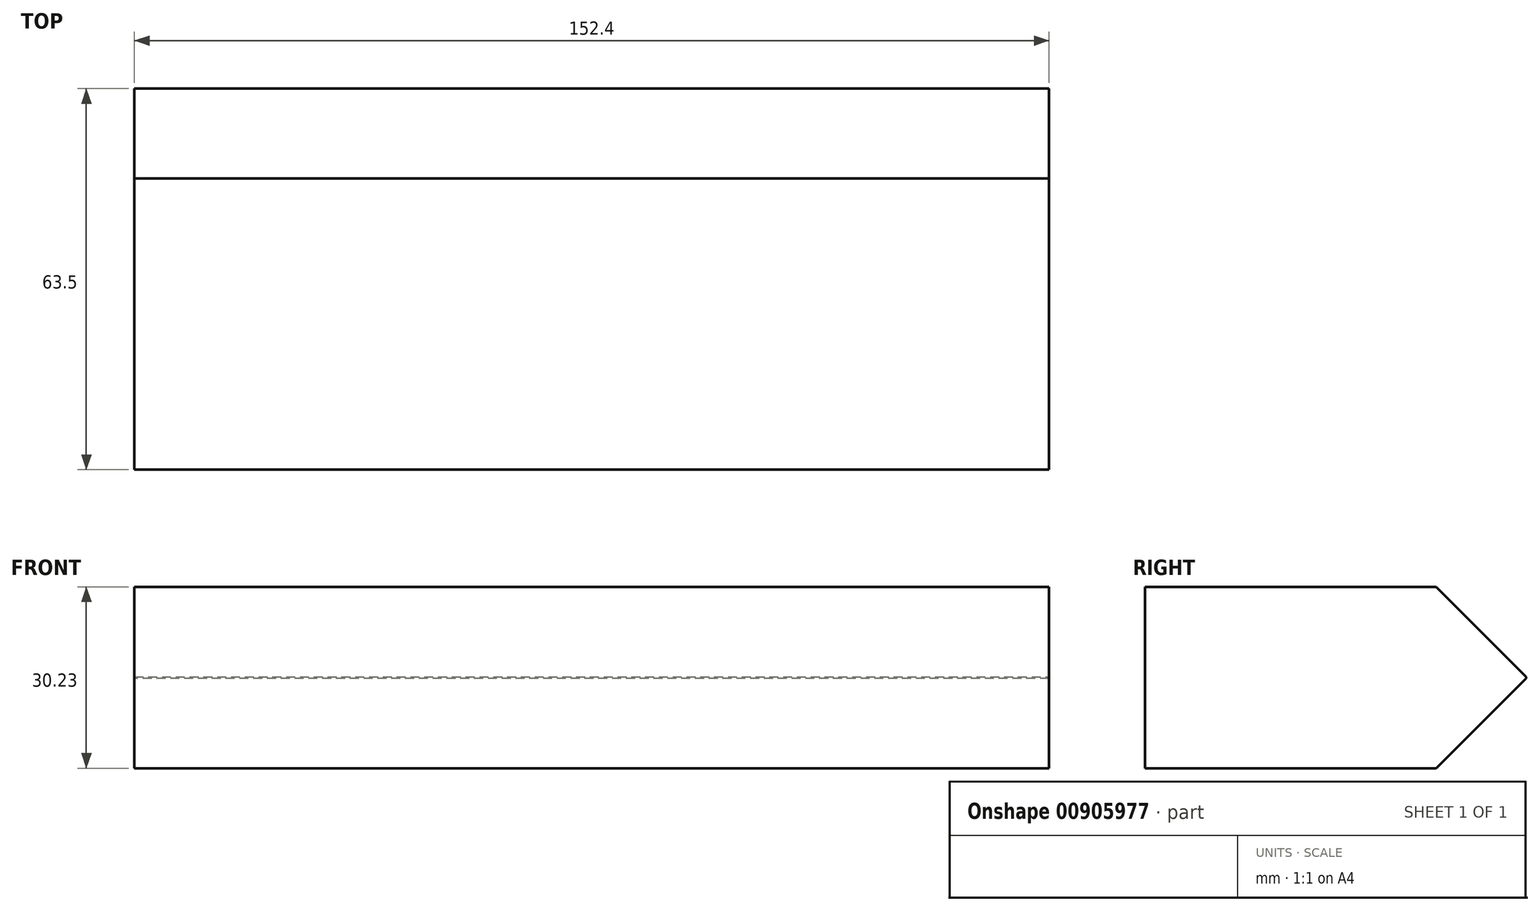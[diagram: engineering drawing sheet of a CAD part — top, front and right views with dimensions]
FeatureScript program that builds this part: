
annotation { "Feature Type Name" : "Feature", "Feature Type Description" : "" }
export const myFeature = defineFeature(function(context is Context, id is Id, definition is map)
    precondition{}
    {
        {
            var Q0;
            Q0=qCreatedBy(makeId("Top.planeOp"),FACE);
            var sketch = newSketch(context, id + "F0", { "sketchPlane" : qUnion([Q0])});
            skLineSegment(sketch, "E0.bottom", {"start": v(-89.64, 44.22) * mm, "end": v(62.76, 44.22) * mm});
            skLineSegment(sketch, "E0.top", {"start": v(-89.64, -19.28) * mm, "end": v(62.76, -19.28) * mm});
            skLineSegment(sketch, "E0.left", {"start": v(-89.64, 44.22) * mm, "end": v(-89.64, -19.28) * mm});
            skLineSegment(sketch, "E0.right", {"start": v(62.76, 44.22) * mm, "end": v(62.76, -19.28) * mm});
            skSolve(sketch);
        }
        {
            var Q0;
            Q0=makeQuery(id+"F0.imprint","IMPRINT",FACE,{"disambiguationData":[TD([[makeQuery(id+"F0.imprint","IMPRINT",EDGE,{"derivedFrom":sQuery(id+"F0.wireOp",EDGE,"E0.bottom")}),-1.0]])]});
            extrude(context, id + "F1", {"entities" : qUnion([Q0]), "depth" : 15.24 * mm, "offsetDistance" : 25.4 * mm});
        }
        {
            var Q0;
            Q0=makeQuery(id+"F1.opExtrude","CAP_EDGE",EDGE,{"disambiguationData":[OSD([sQuery(id+"F0.wireOp",EDGE,"E0.bottom")])],"isStart":false});
            chamfer(context, id + "F2", {"entities" : qUnion([Q0]), "width" : 15 * mm, "tangentPropagation" : true});
        }
        {
            var Q0;
            Q0=makeQuery(id+"F1.opExtrude","CAP_FACE",FACE,{"disambiguationData":[OSD([sQuery(id+"F0.wireOp",EDGE,"E0.bottom"),sQuery(id+"F0.wireOp",EDGE,"E0.top"),sQuery(id+"F0.wireOp",EDGE,"E0.left"),sQuery(id+"F0.wireOp",EDGE,"E0.right")])],"isStart":true});
            extrude(context, id + "F3", {"entities" : qUnion([Q0]), "operationType" : NewBodyOperationType.ADD, "depth" : 15 * mm, "offsetDistance" : 25.4 * mm});
        }
        {
            var Q0;
            Q0=makeQuery(id+"F3.opExtrude","CAP_EDGE",EDGE,{"disambiguationData":[OSD([sQuery(id+"F0.wireOp",EDGE,"E0.bottom")])],"isStart":false});
            chamfer(context, id + "F4", {"entities" : qUnion([Q0]), "width" : 15 * mm, "tangentPropagation" : true});
        }
    });
